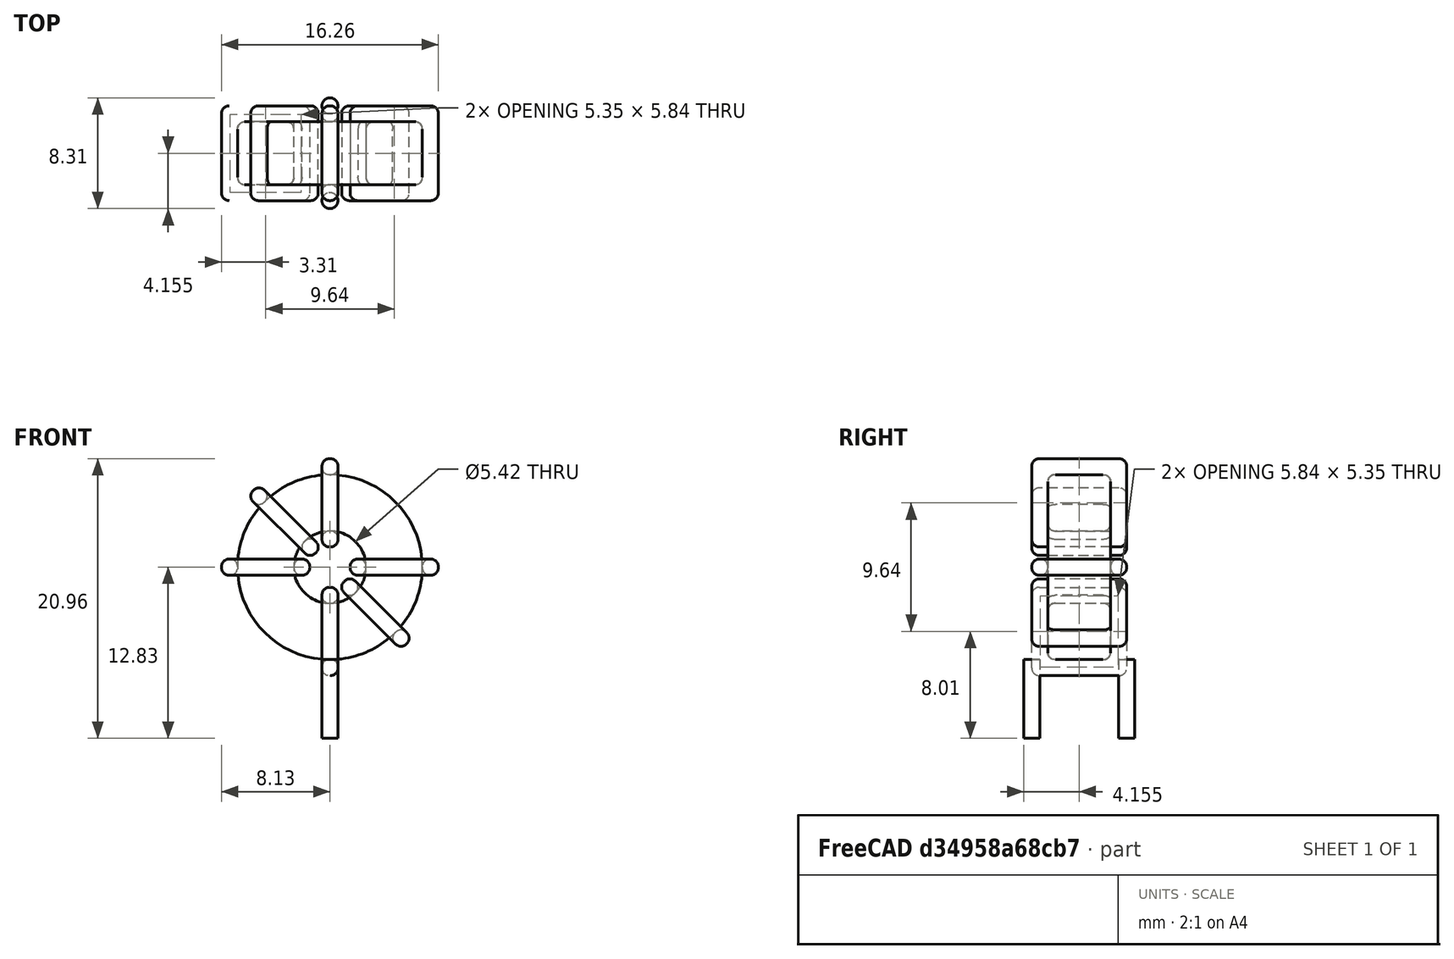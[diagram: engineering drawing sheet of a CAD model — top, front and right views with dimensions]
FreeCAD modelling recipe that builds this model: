
FCSTD DOCUMENT  (FreeCAD 0.16R6703 (Git))
Label: L_Toroid_Vertical_L16.3mm_W7.1mm_P7.11mm_Pulse_H
License: All rights reserved
LicenseURL: http://en.wikipedia.org/wiki/All_rights_reserved
objects: Sketcher::SketchObject×6, PartDesign::Pad×6, PartDesign::Fillet×5, Spreadsheet::Sheet×1
note: 23 computed .brp shape members not serialized (recipe doc carries the construction recipe); baked Part::Feature solids carry a one-line shape summary decoded from their .brp

FEATURE [Spreadsheet::Sheet] Spreadsheet  label="dimensions"
  cells = A1=Wx; B1(Wx)=16.26; C1(WW)=5.420000000000001; D1=16.26; A2=Wy; B2(Wy)=7.11; D2=7.11; A3=RM; B3(RMx)=7.11; C3(RMy)=0; A4=d_wire; B4(d_wire)=1.2; A5=H; B5(H)=16.26; A6=offsetx; B6(offsetx)=8.130000000000001
FEATURE [Sketcher::SketchObject] Sketch
  Placement = pos=(0,-3.555,0) rot=(1,0,0;1.5708rad)
  expr: Placement.Base.y = -Spreadsheet.RMx / 2
  expr: Constraints[0] = Spreadsheet.Wx / 2 - Spreadsheet.d_wire
  expr: Constraints[4] = Spreadsheet.WW / 2
  expr: Constraints[2] = Spreadsheet.Wx / 2 + Spreadsheet.d_wire + 0.5
  sketch-geometry (2):
    g0: Circle CenterX=0 CenterY=9.83 CenterZ=0 NormalX=0 NormalY=0 NormalZ=1 Radius=6.93
    g1: Circle CenterX=0 CenterY=9.83 CenterZ=0 NormalX=0 NormalY=0 NormalZ=1 Radius=2.71
  constraints (5):
    c: Radius(g0) = 6.93
    c: DistanceX(g-1,g0) = 0
    c: DistanceY(g-1,g0) = 9.83
    c: Coincident(g1,g0)
    c: Radius(g1) = 2.71
FEATURE [PartDesign::Pad] Pad
  Length = 4.71
  Length2 = 100
  Midplane = true
  Placement = pos=(0,-3.555,0) rot=(1,0,0;1.5708rad)
  Sketch = -> Sketch
  Type = 0
  expr: Length = Spreadsheet.Wy - 2 * Spreadsheet.d_wire
FEATURE [Sketcher::SketchObject] Sketch001
  Placement = pos=(0,0,1.7) rot=(0,0,1;0rad)
  expr: Placement.Base.z = 0.5 + Spreadsheet.d_wire
  expr: Constraints[4] = Spreadsheet.RMy
  expr: Constraints[2] = -Spreadsheet.RMx
  expr: Constraints[1] = Spreadsheet.d_wire / 2
  sketch-geometry (2):
    g0: Circle CenterX=0 CenterY=0 CenterZ=0 NormalX=0 NormalY=0 NormalZ=1 Radius=0.6
    g1: Circle CenterX=0 CenterY=-7.11 CenterZ=0 NormalX=0 NormalY=0 NormalZ=1 Radius=0.6
  constraints (5):
    c: Equal(g0,g1)
    c: Radius(g0) = 0.6
    c: DistanceY(g-1,g1) = -7.11
    c: Coincident(g0,g-1)
    c: DistanceX(g-1,g1) = 0
FEATURE [PartDesign::Pad] Pad001
  Length = 1.2
  Length2 = 4.7
  Placement = pos=(0,0,1.7) rot=(0,0,1;0rad)
  Reversed = true
  Sketch = -> Sketch001
  Type = 4
  expr: Length2 = 3.5 + Spreadsheet.d_wire
  expr: Length = Spreadsheet.d_wire
FEATURE [PartDesign::Fillet] Fillet
  Base = -> Pad [Edge6,Edge3,Edge2]
  Placement = pos=(0,-3.555,0) rot=(1,0,0;1.5708rad)
  Radius = 0.5
FEATURE [Sketcher::SketchObject] Sketch003
  Placement = pos=(0,0,9.83) rot=(1,0,0;3.14159rad)
  expr: Constraints[18] = Spreadsheet.d_wire
  expr: Constraints[16] = Spreadsheet.d_wire
  expr: Constraints[19] = Spreadsheet.d_wire
  expr: Constraints[17] = Spreadsheet.d_wire
  expr: Placement.Base.y = -1 * (Spreadsheet.RMx - Spreadsheet.Wy) / 2
  expr: Constraints[21] = (Spreadsheet.Wx - Spreadsheet.WW) / 2 - Spreadsheet.d_wire
  expr: Constraints[22] = Spreadsheet.Wx / 2 - Spreadsheet.d_wire
  expr: Constraints[43] = Spreadsheet.d_wire
  expr: Constraints[48] = Spreadsheet.Wx - Spreadsheet.d_wire * 2
  expr: Constraints[49] = Spreadsheet.Wy
  expr: Placement.Base.z = Spreadsheet.Wx / 2 + Spreadsheet.d_wire + 0.5
  sketch-geometry (16):
    g0: LineSegment StartX=-1.51 StartY=0 StartZ=0 EndX=-8.13 EndY=0 EndZ=0
    g1: LineSegment StartX=-8.13 StartY=0 StartZ=0 EndX=-8.13 EndY=7.11 EndZ=0
    g2: LineSegment StartX=-8.13 StartY=7.11 StartZ=0 EndX=-1.51 EndY=7.11 EndZ=0
    g3: LineSegment StartX=-1.51 StartY=7.11 StartZ=0 EndX=-1.51 EndY=0 EndZ=0
    g4: LineSegment StartX=-6.93 StartY=5.91 StartZ=0 EndX=-2.71 EndY=5.91 EndZ=0
    g5: LineSegment StartX=-2.71 StartY=5.91 StartZ=0 EndX=-2.71 EndY=1.2 EndZ=0
    g6: LineSegment StartX=-2.71 StartY=1.2 StartZ=0 EndX=-6.93 EndY=1.2 EndZ=0
    g7: LineSegment StartX=-6.93 StartY=1.2 StartZ=0 EndX=-6.93 EndY=5.91 EndZ=0
    g8: LineSegment StartX=1.51 StartY=7.11 StartZ=0 EndX=8.13 EndY=7.11 EndZ=0
    g9: LineSegment StartX=8.13 StartY=7.11 StartZ=0 EndX=8.13 EndY=0 EndZ=0
    g10: LineSegment StartX=8.13 StartY=0 StartZ=0 EndX=1.51 EndY=0 EndZ=0
    g11: LineSegment StartX=1.51 StartY=0 StartZ=0 EndX=1.51 EndY=7.11 EndZ=0
    g12: LineSegment StartX=2.71 StartY=5.91 StartZ=0 EndX=6.93 EndY=5.91 EndZ=0
    g13: LineSegment StartX=6.93 StartY=5.91 StartZ=0 EndX=6.93 EndY=1.2 EndZ=0
    g14: LineSegment StartX=6.93 StartY=1.2 StartZ=0 EndX=2.71 EndY=1.2 EndZ=0
    g15: LineSegment StartX=2.71 StartY=1.2 StartZ=0 EndX=2.71 EndY=5.91 EndZ=0
  constraints (50):
    c: Horizontal(g0)
    c: Coincident(g1,g0)
    c: Vertical(g1)
    c: Coincident(g2,g1)
    c: Horizontal(g2)
    c: Coincident(g3,g2)
    c: Coincident(g3,g0)
    c: Vertical(g3)
    c: Coincident(g4,g5)
    c: Coincident(g5,g6)
    c: Coincident(g6,g7)
    c: Coincident(g7,g4)
    c: Horizontal(g4)
    c: Horizontal(g6)
    c: Vertical(g5)
    c: Vertical(g7)
    c: DistanceX(g1,g4) = 1.2
    c: DistanceY(g4,g1) = 1.2
    c: DistanceX(g5,g0) = 1.2
    c: DistanceY(g0,g5) = 1.2
    c: DistanceY(g-1,g0) = 0
    c: DistanceX(g6,g6) = 4.22
    c: DistanceX(g6,g-1) = 6.93
    c: Coincident(g8,g9)
    c: Coincident(g9,g10)
    c: Coincident(g10,g11)
    c: Coincident(g11,g8)
    c: Horizontal(g8)
    c: Horizontal(g10)
    c: Vertical(g9)
    c: Vertical(g11)
    c: Coincident(g12,g13)
    c: Coincident(g13,g14)
    c: Coincident(g14,g15)
    c: Coincident(g15,g12)
    c: Horizontal(g12)
    c: Horizontal(g14)
    c: Vertical(g13)
    c: Vertical(g15)
    c: DistanceY(g8,g2) = 0
    c: DistanceY(g10,g0) = 0
    c: DistanceY(g14,g5) = 0
    c: DistanceY(g12,g4) = 0
    c: DistanceX(g8,g12) = 1.2
    c: Equal(g8,g2)
    c: Equal(g12,g4)
    c: Equal(g9,g1)
    c: Equal(g13,g7)
    c: DistanceX(g4,g12) = 13.86
    c: DistanceY(g0,g1) = 7.11
FEATURE [PartDesign::Pad] Pad002
  Length = 1.2
  Length2 = 100
  Midplane = true
  Placement = pos=(0,0,9.83) rot=(1,0,0;3.14159rad)
  Sketch = -> Sketch003
  Type = 0
  expr: Length = Spreadsheet.d_wire
FEATURE [PartDesign::Fillet] Fillet001
  Base = -> Pad002 [Edge38,Edge41,Edge42,Edge43,Edge29,Edge32,Edge33,Edge34,Edge25,Edge35,Edge36,Edge13,Edge14,Edge15,Edge16,Edge17,Edge18,Edge19,Edge1,Edge2,Edge3,Edge4,Edge5,Edge6,Edge7,Edge37,Edge39,Edge40,Edge20,Edge23,Edge24,Edge21,Edge22,Edge8,Edge9,Edge10,Edge11,Edge12,Edge26,Edge27,+8 more]
  Placement = pos=(0,0,9.83) rot=(1,0,0;3.14159rad)
  Radius = 0.564
  expr: Radius = Spreadsheet.d_wire * 0.47
FEATURE [Sketcher::SketchObject] Sketch004
  Placement = pos=(0,0,9.83) rot=(0.92388,0,0.382683;3.14159rad)
  expr: Constraints[18] = Spreadsheet.d_wire
  expr: Constraints[16] = Spreadsheet.d_wire
  expr: Constraints[19] = Spreadsheet.d_wire
  expr: Constraints[17] = Spreadsheet.d_wire
  expr: Placement.Base.y = -1 * (Spreadsheet.RMx - Spreadsheet.Wy) / 2
  expr: Constraints[21] = (Spreadsheet.Wx - Spreadsheet.WW) / 2 - Spreadsheet.d_wire
  expr: Constraints[22] = Spreadsheet.Wx / 2 - Spreadsheet.d_wire
  expr: Constraints[43] = Spreadsheet.d_wire
  expr: Constraints[48] = Spreadsheet.Wx - 2 * Spreadsheet.d_wire
  expr: Constraints[49] = Spreadsheet.Wy
  expr: Placement.Base.z = Spreadsheet.Wx / 2 + Spreadsheet.d_wire + 0.5
  sketch-geometry (16):
    g0: LineSegment StartX=-1.51 StartY=0 StartZ=0 EndX=-8.13 EndY=0 EndZ=0
    g1: LineSegment StartX=-8.13 StartY=0 StartZ=0 EndX=-8.13 EndY=7.11 EndZ=0
    g2: LineSegment StartX=-8.13 StartY=7.11 StartZ=0 EndX=-1.51 EndY=7.11 EndZ=0
    g3: LineSegment StartX=-1.51 StartY=7.11 StartZ=0 EndX=-1.51 EndY=0 EndZ=0
    g4: LineSegment StartX=-6.93 StartY=5.91 StartZ=0 EndX=-2.71 EndY=5.91 EndZ=0
    g5: LineSegment StartX=-2.71 StartY=5.91 StartZ=0 EndX=-2.71 EndY=1.2 EndZ=0
    g6: LineSegment StartX=-2.71 StartY=1.2 StartZ=0 EndX=-6.93 EndY=1.2 EndZ=0
    g7: LineSegment StartX=-6.93 StartY=1.2 StartZ=0 EndX=-6.93 EndY=5.91 EndZ=0
    g8: LineSegment StartX=1.51 StartY=7.11 StartZ=0 EndX=8.13 EndY=7.11 EndZ=0
    g9: LineSegment StartX=8.13 StartY=7.11 StartZ=0 EndX=8.13 EndY=0 EndZ=0
    g10: LineSegment StartX=8.13 StartY=0 StartZ=0 EndX=1.51 EndY=0 EndZ=0
    g11: LineSegment StartX=1.51 StartY=0 StartZ=0 EndX=1.51 EndY=7.11 EndZ=0
    g12: LineSegment StartX=2.71 StartY=5.91 StartZ=0 EndX=6.93 EndY=5.91 EndZ=0
    g13: LineSegment StartX=6.93 StartY=5.91 StartZ=0 EndX=6.93 EndY=1.2 EndZ=0
    g14: LineSegment StartX=6.93 StartY=1.2 StartZ=0 EndX=2.71 EndY=1.2 EndZ=0
    g15: LineSegment StartX=2.71 StartY=1.2 StartZ=0 EndX=2.71 EndY=5.91 EndZ=0
  constraints (50):
    c: Horizontal(g0)
    c: Coincident(g1,g0)
    c: Vertical(g1)
    c: Coincident(g2,g1)
    c: Horizontal(g2)
    c: Coincident(g3,g2)
    c: Coincident(g3,g0)
    c: Vertical(g3)
    c: Coincident(g4,g5)
    c: Coincident(g5,g6)
    c: Coincident(g6,g7)
    c: Coincident(g7,g4)
    c: Horizontal(g4)
    c: Horizontal(g6)
    c: Vertical(g5)
    c: Vertical(g7)
    c: DistanceX(g1,g4) = 1.2
    c: DistanceY(g4,g1) = 1.2
    c: DistanceX(g5,g0) = 1.2
    c: DistanceY(g0,g5) = 1.2
    c: DistanceY(g-1,g0) = 0
    c: DistanceX(g6,g6) = 4.22
    c: DistanceX(g6,g-1) = 6.93
    c: Coincident(g8,g9)
    c: Coincident(g9,g10)
    c: Coincident(g10,g11)
    c: Coincident(g11,g8)
    c: Horizontal(g8)
    c: Horizontal(g10)
    c: Vertical(g9)
    c: Vertical(g11)
    c: Coincident(g12,g13)
    c: Coincident(g13,g14)
    c: Coincident(g14,g15)
    c: Coincident(g15,g12)
    c: Horizontal(g12)
    c: Horizontal(g14)
    c: Vertical(g13)
    c: Vertical(g15)
    c: DistanceY(g8,g2) = 0
    c: DistanceY(g10,g0) = 0
    c: DistanceY(g14,g5) = 0
    c: DistanceY(g12,g4) = 0
    c: DistanceX(g8,g12) = 1.2
    c: Equal(g8,g2)
    c: Equal(g12,g4)
    c: Equal(g9,g1)
    c: Equal(g13,g7)
    c: DistanceX(g4,g12) = 13.86
    c: DistanceY(g0,g1) = 7.11
FEATURE [PartDesign::Pad] Pad003
  Length = 1.2
  Length2 = 100
  Midplane = true
  Placement = pos=(0,0,9.83) rot=(0.92388,0,0.382683;3.14159rad)
  Sketch = -> Sketch004
  Type = 0
  expr: Length = Spreadsheet.d_wire
FEATURE [PartDesign::Fillet] Fillet002
  Base = -> Pad003 [Edge38,Edge41,Edge42,Edge43,Edge29,Edge32,Edge33,Edge34,Edge25,Edge35,Edge36,Edge13,Edge14,Edge15,Edge16,Edge17,Edge18,Edge19,Edge1,Edge2,Edge3,Edge4,Edge5,Edge6,Edge7,Edge37,Edge39,Edge40,Edge20,Edge23,Edge24,Edge21,Edge22,Edge8,Edge9,Edge10,Edge11,Edge12,Edge26,Edge27,+8 more]
  Placement = pos=(0,0,9.83) rot=(0.92388,0,0.382683;3.14159rad)
  Radius = 0.564
  expr: Radius = Spreadsheet.d_wire * 0.47
FEATURE [Sketcher::SketchObject] Sketch005
  Placement = pos=(0,0,9.83) rot=(0.92388,0,-0.382683;3.14159rad)
  expr: Constraints[18] = Spreadsheet.d_wire
  expr: Constraints[16] = Spreadsheet.d_wire
  expr: Constraints[19] = Spreadsheet.d_wire
  expr: Constraints[17] = Spreadsheet.d_wire
  expr: Placement.Base.y = -1 * (Spreadsheet.RMx - Spreadsheet.Wy) / 2
  expr: Constraints[21] = (Spreadsheet.Wx - Spreadsheet.WW) / 2 - Spreadsheet.d_wire
  expr: Constraints[22] = Spreadsheet.Wx / 2 - Spreadsheet.d_wire
  expr: Constraints[43] = Spreadsheet.d_wire
  expr: Constraints[48] = Spreadsheet.Wx - 2 * Spreadsheet.d_wire
  expr: Constraints[49] = Spreadsheet.Wy
  expr: Placement.Base.z = Spreadsheet.Wx / 2 + Spreadsheet.d_wire + 0.5
  sketch-geometry (16):
    g0: LineSegment StartX=-1.51 StartY=0 StartZ=0 EndX=-8.13 EndY=0 EndZ=0
    g1: LineSegment StartX=-8.13 StartY=0 StartZ=0 EndX=-8.13 EndY=7.11 EndZ=0
    g2: LineSegment StartX=-8.13 StartY=7.11 StartZ=0 EndX=-1.51 EndY=7.11 EndZ=0
    g3: LineSegment StartX=-1.51 StartY=7.11 StartZ=0 EndX=-1.51 EndY=0 EndZ=0
    g4: LineSegment StartX=-6.93 StartY=5.91 StartZ=0 EndX=-2.71 EndY=5.91 EndZ=0
    g5: LineSegment StartX=-2.71 StartY=5.91 StartZ=0 EndX=-2.71 EndY=1.2 EndZ=0
    g6: LineSegment StartX=-2.71 StartY=1.2 StartZ=0 EndX=-6.93 EndY=1.2 EndZ=0
    g7: LineSegment StartX=-6.93 StartY=1.2 StartZ=0 EndX=-6.93 EndY=5.91 EndZ=0
    g8: LineSegment StartX=1.51 StartY=7.11 StartZ=0 EndX=8.13 EndY=7.11 EndZ=0
    g9: LineSegment StartX=8.13 StartY=7.11 StartZ=0 EndX=8.13 EndY=0 EndZ=0
    g10: LineSegment StartX=8.13 StartY=0 StartZ=0 EndX=1.51 EndY=0 EndZ=0
    g11: LineSegment StartX=1.51 StartY=0 StartZ=0 EndX=1.51 EndY=7.11 EndZ=0
    g12: LineSegment StartX=2.71 StartY=5.91 StartZ=0 EndX=6.93 EndY=5.91 EndZ=0
    g13: LineSegment StartX=6.93 StartY=5.91 StartZ=0 EndX=6.93 EndY=1.2 EndZ=0
    g14: LineSegment StartX=6.93 StartY=1.2 StartZ=0 EndX=2.71 EndY=1.2 EndZ=0
    g15: LineSegment StartX=2.71 StartY=1.2 StartZ=0 EndX=2.71 EndY=5.91 EndZ=0
  constraints (50):
    c: Horizontal(g0)
    c: Coincident(g1,g0)
    c: Vertical(g1)
    c: Coincident(g2,g1)
    c: Horizontal(g2)
    c: Coincident(g3,g2)
    c: Coincident(g3,g0)
    c: Vertical(g3)
    c: Coincident(g4,g5)
    c: Coincident(g5,g6)
    c: Coincident(g6,g7)
    c: Coincident(g7,g4)
    c: Horizontal(g4)
    c: Horizontal(g6)
    c: Vertical(g5)
    c: Vertical(g7)
    c: DistanceX(g1,g4) = 1.2
    c: DistanceY(g4,g1) = 1.2
    c: DistanceX(g5,g0) = 1.2
    c: DistanceY(g0,g5) = 1.2
    c: DistanceY(g-1,g0) = 0
    c: DistanceX(g6,g6) = 4.22
    c: DistanceX(g6,g-1) = 6.93
    c: Coincident(g8,g9)
    c: Coincident(g9,g10)
    c: Coincident(g10,g11)
    c: Coincident(g11,g8)
    c: Horizontal(g8)
    c: Horizontal(g10)
    c: Vertical(g9)
    c: Vertical(g11)
    c: Coincident(g12,g13)
    c: Coincident(g13,g14)
    c: Coincident(g14,g15)
    c: Coincident(g15,g12)
    c: Horizontal(g12)
    c: Horizontal(g14)
    c: Vertical(g13)
    c: Vertical(g15)
    c: DistanceY(g8,g2) = 0
    c: DistanceY(g10,g0) = 0
    c: DistanceY(g14,g5) = 0
    c: DistanceY(g12,g4) = 0
    c: DistanceX(g8,g12) = 1.2
    c: Equal(g8,g2)
    c: Equal(g12,g4)
    c: Equal(g9,g1)
    c: Equal(g13,g7)
    c: DistanceX(g4,g12) = 13.86
    c: DistanceY(g0,g1) = 7.11
FEATURE [PartDesign::Pad] Pad004
  Length = 1.2
  Length2 = 100
  Midplane = true
  Placement = pos=(0,0,9.83) rot=(0.92388,0,-0.382683;3.14159rad)
  Sketch = -> Sketch005
  Type = 0
  expr: Length = Spreadsheet.d_wire
FEATURE [PartDesign::Fillet] Fillet003
  Base = -> Pad004 [Edge38,Edge41,Edge42,Edge43,Edge29,Edge32,Edge33,Edge34,Edge25,Edge35,Edge36,Edge13,Edge14,Edge15,Edge16,Edge17,Edge18,Edge19,Edge1,Edge2,Edge3,Edge4,Edge5,Edge6,Edge7,Edge37,Edge39,Edge40,Edge20,Edge23,Edge24,Edge21,Edge22,Edge8,Edge9,Edge10,Edge11,Edge12,Edge26,Edge27,+8 more]
  Placement = pos=(0,0,9.83) rot=(0.92388,0,-0.382683;3.14159rad)
  Radius = 0.564
  expr: Radius = Spreadsheet.d_wire * 0.47
FEATURE [Sketcher::SketchObject] Sketch006
  Placement = pos=(0,0,9.83) rot=(0.707107,0,0.707107;3.14159rad)
  expr: Constraints[18] = Spreadsheet.d_wire
  expr: Constraints[16] = Spreadsheet.d_wire
  expr: Constraints[19] = Spreadsheet.d_wire
  expr: Constraints[17] = Spreadsheet.d_wire
  expr: Placement.Base.y = -1 * (Spreadsheet.RMx - Spreadsheet.Wy) / 2
  expr: Constraints[21] = (Spreadsheet.Wx - Spreadsheet.WW) / 2 - Spreadsheet.d_wire
  expr: Constraints[22] = Spreadsheet.Wx / 2 - Spreadsheet.d_wire
  expr: Constraints[43] = Spreadsheet.d_wire
  expr: Constraints[48] = Spreadsheet.Wx - Spreadsheet.d_wire * 2
  expr: Constraints[49] = Spreadsheet.Wy
  expr: Placement.Base.z = Spreadsheet.Wx / 2 + Spreadsheet.d_wire + 0.5
  sketch-geometry (16):
    g0: LineSegment StartX=-1.51 StartY=0 StartZ=0 EndX=-8.13 EndY=0 EndZ=0
    g1: LineSegment StartX=-8.13 StartY=0 StartZ=0 EndX=-8.13 EndY=7.11 EndZ=0
    g2: LineSegment StartX=-8.13 StartY=7.11 StartZ=0 EndX=-1.51 EndY=7.11 EndZ=0
    g3: LineSegment StartX=-1.51 StartY=7.11 StartZ=0 EndX=-1.51 EndY=0 EndZ=0
    g4: LineSegment StartX=-6.93 StartY=5.91 StartZ=0 EndX=-2.71 EndY=5.91 EndZ=0
    g5: LineSegment StartX=-2.71 StartY=5.91 StartZ=0 EndX=-2.71 EndY=1.2 EndZ=0
    g6: LineSegment StartX=-2.71 StartY=1.2 StartZ=0 EndX=-6.93 EndY=1.2 EndZ=0
    g7: LineSegment StartX=-6.93 StartY=1.2 StartZ=0 EndX=-6.93 EndY=5.91 EndZ=0
    g8: LineSegment StartX=1.51 StartY=7.11 StartZ=0 EndX=8.13 EndY=7.11 EndZ=0
    g9: LineSegment StartX=8.13 StartY=7.11 StartZ=0 EndX=8.13 EndY=0 EndZ=0
    g10: LineSegment StartX=8.13 StartY=0 StartZ=0 EndX=1.51 EndY=0 EndZ=0
    g11: LineSegment StartX=1.51 StartY=0 StartZ=0 EndX=1.51 EndY=7.11 EndZ=0
    g12: LineSegment StartX=2.71 StartY=5.91 StartZ=0 EndX=6.93 EndY=5.91 EndZ=0
    g13: LineSegment StartX=6.93 StartY=5.91 StartZ=0 EndX=6.93 EndY=1.2 EndZ=0
    g14: LineSegment StartX=6.93 StartY=1.2 StartZ=0 EndX=2.71 EndY=1.2 EndZ=0
    g15: LineSegment StartX=2.71 StartY=1.2 StartZ=0 EndX=2.71 EndY=5.91 EndZ=0
  constraints (50):
    c: Horizontal(g0)
    c: Coincident(g1,g0)
    c: Vertical(g1)
    c: Coincident(g2,g1)
    c: Horizontal(g2)
    c: Coincident(g3,g2)
    c: Coincident(g3,g0)
    c: Vertical(g3)
    c: Coincident(g4,g5)
    c: Coincident(g5,g6)
    c: Coincident(g6,g7)
    c: Coincident(g7,g4)
    c: Horizontal(g4)
    c: Horizontal(g6)
    c: Vertical(g5)
    c: Vertical(g7)
    c: DistanceX(g1,g4) = 1.2
    c: DistanceY(g4,g1) = 1.2
    c: DistanceX(g5,g0) = 1.2
    c: DistanceY(g0,g5) = 1.2
    c: DistanceY(g-1,g0) = 0
    c: DistanceX(g6,g6) = 4.22
    c: DistanceX(g6,g-1) = 6.93
    c: Coincident(g8,g9)
    c: Coincident(g9,g10)
    c: Coincident(g10,g11)
    c: Coincident(g11,g8)
    c: Horizontal(g8)
    c: Horizontal(g10)
    c: Vertical(g9)
    c: Vertical(g11)
    c: Coincident(g12,g13)
    c: Coincident(g13,g14)
    c: Coincident(g14,g15)
    c: Coincident(g15,g12)
    c: Horizontal(g12)
    c: Horizontal(g14)
    c: Vertical(g13)
    c: Vertical(g15)
    c: DistanceY(g8,g2) = 0
    c: DistanceY(g10,g0) = 0
    c: DistanceY(g14,g5) = 0
    c: DistanceY(g12,g4) = 0
    c: DistanceX(g8,g12) = 1.2
    c: Equal(g8,g2)
    c: Equal(g12,g4)
    c: Equal(g9,g1)
    c: Equal(g13,g7)
    c: DistanceX(g4,g12) = 13.86
    c: DistanceY(g0,g1) = 7.11
FEATURE [PartDesign::Pad] Pad005
  Length = 1.2
  Length2 = 100
  Midplane = true
  Placement = pos=(0,0,9.83) rot=(0.707107,0,0.707107;3.14159rad)
  Sketch = -> Sketch006
  Type = 0
  expr: Length = Spreadsheet.d_wire
FEATURE [PartDesign::Fillet] Fillet004
  Base = -> Pad005 [Edge38,Edge41,Edge42,Edge43,Edge29,Edge32,Edge33,Edge34,Edge25,Edge35,Edge36,Edge13,Edge14,Edge15,Edge16,Edge17,Edge18,Edge19,Edge1,Edge2,Edge3,Edge4,Edge5,Edge6,Edge7,Edge37,Edge39,Edge40,Edge20,Edge23,Edge24,Edge21,Edge22,Edge8,Edge9,Edge10,Edge11,Edge12,Edge26,Edge27,+8 more]
  Placement = pos=(0,0,9.83) rot=(0.707107,0,0.707107;3.14159rad)
  Radius = 0.564
  expr: Radius = Spreadsheet.d_wire * 0.47
